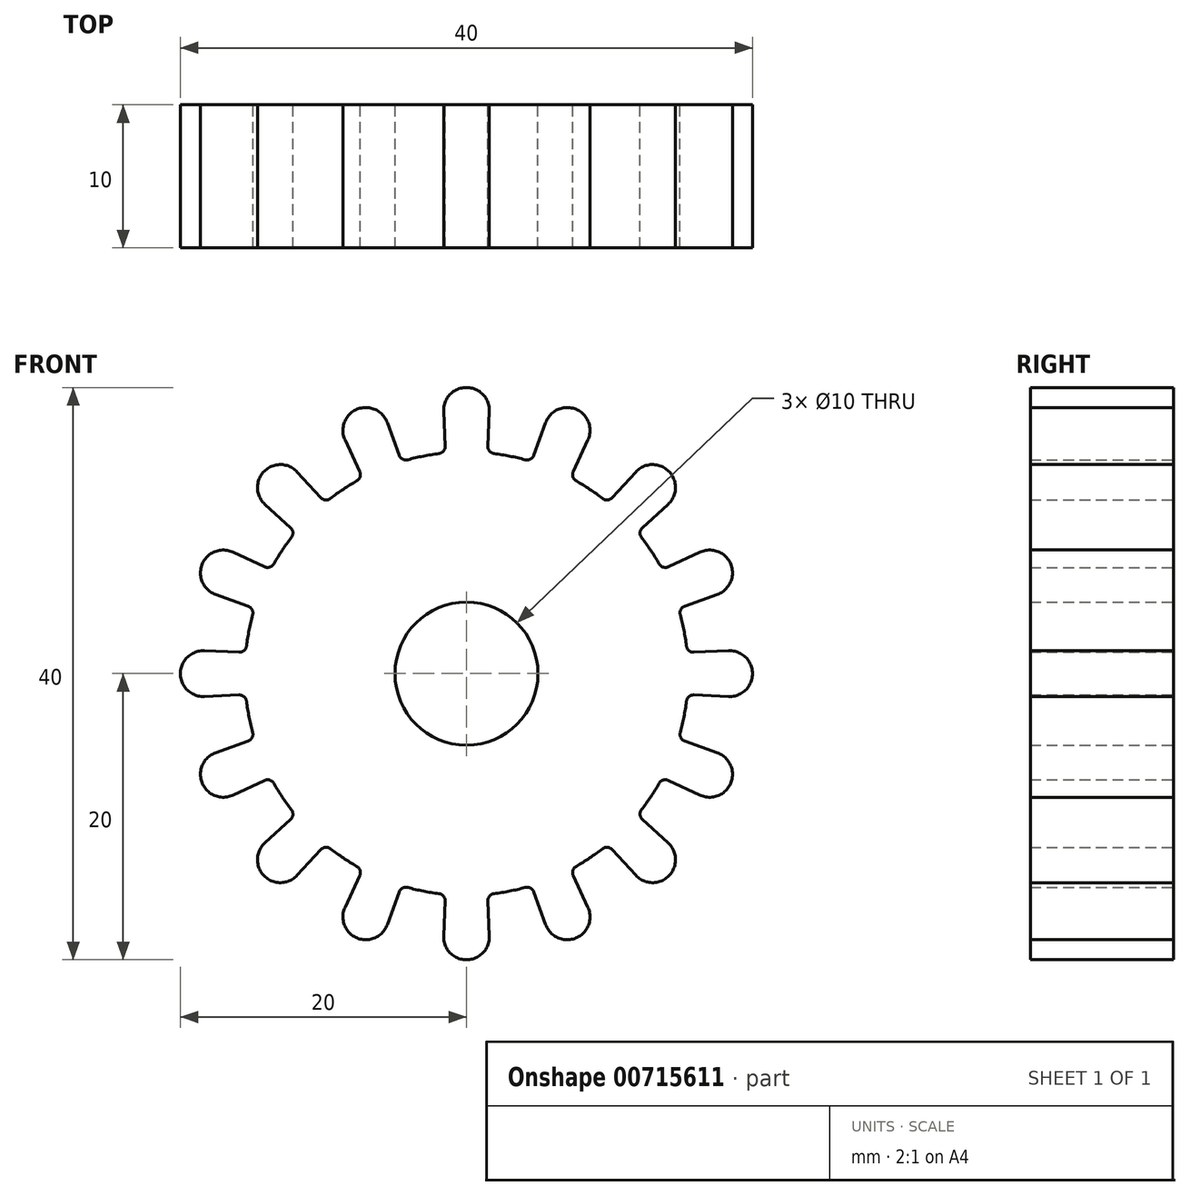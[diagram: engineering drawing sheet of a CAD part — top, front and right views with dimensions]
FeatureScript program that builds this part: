
annotation { "Feature Type Name" : "Feature", "Feature Type Description" : "" }
export const myFeature = defineFeature(function(context is Context, id is Id, definition is map)
    precondition{}
    {
        {
            var Q0;
            Q0=qCreatedBy(makeId("Front.planeOp"),FACE);
            var sketch = newSketch(context, id + "F0", { "sketchPlane" : qUnion([Q0])});
            skCircle(sketch, "E0", {"center": v(0, 0) * mm, "radius": 5 * mm});
            skCircle(sketch, "E1", {"center": v(0, 0) * mm, "radius": 15.5 * mm});
            skCircle(sketch, "E2", {"center": v(0, 0) * mm, "radius": 18.4 * mm, "construction": true});
            skCircle(sketch, "E3", {"center": v(0, 18.4) * mm, "radius": 1.6 * mm});
            skLineSegment(sketch, "E4", {"start": v(-1.6, 18.33) * mm, "end": v(-1.5, 15.9) * mm});
            skLineSegment(sketch, "E5", {"start": v(1.6, 18.33) * mm, "end": v(1.5, 15.9) * mm});
            skArc(sketch, "E6", {"start": v(-1.93, 15.38) * mm, "mid": v(-1.61, 15.55) * mm, "end": v(-1.5, 15.9) * mm});
            skArc(sketch, "E7", {"start": v(1.5, 15.9) * mm, "mid": v(1.61, 15.55) * mm, "end": v(1.93, 15.38) * mm});
            skCircle(sketch, "E8.1.0", {"center": v(-7.04, 17) * mm, "radius": 1.6 * mm});
            skLineSegment(sketch, "E8.1.1", {"start": v(-5.54, 17.55) * mm, "end": v(-4.7, 15.26) * mm});
            skLineSegment(sketch, "E8.1.2", {"start": v(-8.5, 16.32) * mm, "end": v(-7.46, 14.12) * mm});
            skArc(sketch, "E8.1.3", {"start": v(-7.67, 13.47) * mm, "mid": v(-7.44, 13.75) * mm, "end": v(-7.46, 14.12) * mm});
            skArc(sketch, "E8.1.4", {"start": v(-4.7, 15.26) * mm, "mid": v(-4.46, 14.99) * mm, "end": v(-4.1, 14.95) * mm});
            skCircle(sketch, "E8.2.0", {"center": v(-13.01, 13.01) * mm, "radius": 1.6 * mm});
            skLineSegment(sketch, "E8.2.1", {"start": v(-11.83, 14.1) * mm, "end": v(-10.19, 12.3) * mm});
            skLineSegment(sketch, "E8.2.2", {"start": v(-14.1, 11.83) * mm, "end": v(-12.3, 10.19) * mm});
            skArc(sketch, "E8.2.3", {"start": v(-12.24, 9.51) * mm, "mid": v(-12.14, 9.86) * mm, "end": v(-12.3, 10.19) * mm});
            skArc(sketch, "E8.2.4", {"start": v(-10.19, 12.3) * mm, "mid": v(-9.86, 12.14) * mm, "end": v(-9.51, 12.24) * mm});
            skCircle(sketch, "E9.1.3.0", {"center": v(-17, 7.04) * mm, "radius": 1.6 * mm});
            skLineSegment(sketch, "E9.2.3.0", {"start": v(-16.32, 8.5) * mm, "end": v(-14.12, 7.46) * mm});
            skLineSegment(sketch, "E9.5.3.0", {"start": v(-17.55, 5.54) * mm, "end": v(-15.26, 4.7) * mm});
            skArc(sketch, "E9.8.3.0", {"start": v(-14.95, 4.1) * mm, "mid": v(-14.99, 4.46) * mm, "end": v(-15.26, 4.7) * mm});
            skArc(sketch, "E9.12.3.0", {"start": v(-14.12, 7.46) * mm, "mid": v(-13.75, 7.44) * mm, "end": v(-13.47, 7.67) * mm});
            skCircle(sketch, "E9.1.4.0", {"center": v(-18.4, 0) * mm, "radius": 1.6 * mm});
            skLineSegment(sketch, "E9.2.4.0", {"start": v(-18.33, 1.6) * mm, "end": v(-15.9, 1.5) * mm});
            skLineSegment(sketch, "E9.5.4.0", {"start": v(-18.33, -1.6) * mm, "end": v(-15.9, -1.5) * mm});
            skArc(sketch, "E9.8.4.0", {"start": v(-15.38, -1.93) * mm, "mid": v(-15.55, -1.61) * mm, "end": v(-15.9, -1.5) * mm});
            skArc(sketch, "E9.12.4.0", {"start": v(-15.9, 1.5) * mm, "mid": v(-15.55, 1.61) * mm, "end": v(-15.38, 1.93) * mm});
            skCircle(sketch, "E9.1.5.0", {"center": v(-17, -7.04) * mm, "radius": 1.6 * mm});
            skLineSegment(sketch, "E9.2.5.0", {"start": v(-17.55, -5.54) * mm, "end": v(-15.26, -4.7) * mm});
            skLineSegment(sketch, "E9.5.5.0", {"start": v(-16.32, -8.5) * mm, "end": v(-14.12, -7.46) * mm});
            skArc(sketch, "E9.8.5.0", {"start": v(-13.47, -7.67) * mm, "mid": v(-13.75, -7.44) * mm, "end": v(-14.12, -7.46) * mm});
            skArc(sketch, "E9.12.5.0", {"start": v(-15.26, -4.7) * mm, "mid": v(-14.99, -4.46) * mm, "end": v(-14.95, -4.1) * mm});
            skCircle(sketch, "E9.1.6.0", {"center": v(-13.01, -13.01) * mm, "radius": 1.6 * mm});
            skLineSegment(sketch, "E9.2.6.0", {"start": v(-14.1, -11.83) * mm, "end": v(-12.3, -10.19) * mm});
            skLineSegment(sketch, "E9.5.6.0", {"start": v(-11.83, -14.1) * mm, "end": v(-10.19, -12.3) * mm});
            skArc(sketch, "E9.8.6.0", {"start": v(-9.51, -12.24) * mm, "mid": v(-9.86, -12.14) * mm, "end": v(-10.19, -12.3) * mm});
            skArc(sketch, "E9.12.6.0", {"start": v(-12.3, -10.19) * mm, "mid": v(-12.14, -9.86) * mm, "end": v(-12.24, -9.51) * mm});
            skCircle(sketch, "E9.1.7.0", {"center": v(-7.04, -17) * mm, "radius": 1.6 * mm});
            skLineSegment(sketch, "E9.2.7.0", {"start": v(-8.5, -16.32) * mm, "end": v(-7.46, -14.12) * mm});
            skLineSegment(sketch, "E9.5.7.0", {"start": v(-5.54, -17.55) * mm, "end": v(-4.7, -15.26) * mm});
            skArc(sketch, "E9.8.7.0", {"start": v(-4.1, -14.95) * mm, "mid": v(-4.46, -14.99) * mm, "end": v(-4.7, -15.26) * mm});
            skArc(sketch, "E9.12.7.0", {"start": v(-7.46, -14.12) * mm, "mid": v(-7.44, -13.75) * mm, "end": v(-7.67, -13.47) * mm});
            skCircle(sketch, "E9.1.8.0", {"center": v(0, -18.4) * mm, "radius": 1.6 * mm});
            skLineSegment(sketch, "E9.2.8.0", {"start": v(-1.6, -18.33) * mm, "end": v(-1.5, -15.9) * mm});
            skLineSegment(sketch, "E9.5.8.0", {"start": v(1.6, -18.33) * mm, "end": v(1.5, -15.9) * mm});
            skArc(sketch, "E9.8.8.0", {"start": v(1.93, -15.38) * mm, "mid": v(1.61, -15.55) * mm, "end": v(1.5, -15.9) * mm});
            skArc(sketch, "E9.12.8.0", {"start": v(-1.5, -15.9) * mm, "mid": v(-1.61, -15.55) * mm, "end": v(-1.93, -15.38) * mm});
            skCircle(sketch, "E9.1.9.0", {"center": v(7.04, -17) * mm, "radius": 1.6 * mm});
            skLineSegment(sketch, "E9.2.9.0", {"start": v(5.54, -17.55) * mm, "end": v(4.7, -15.26) * mm});
            skLineSegment(sketch, "E9.5.9.0", {"start": v(8.5, -16.32) * mm, "end": v(7.46, -14.12) * mm});
            skArc(sketch, "E9.8.9.0", {"start": v(7.67, -13.47) * mm, "mid": v(7.44, -13.75) * mm, "end": v(7.46, -14.12) * mm});
            skArc(sketch, "E9.12.9.0", {"start": v(4.7, -15.26) * mm, "mid": v(4.46, -14.99) * mm, "end": v(4.1, -14.95) * mm});
            skCircle(sketch, "E9.1.10.0", {"center": v(13.01, -13.01) * mm, "radius": 1.6 * mm});
            skLineSegment(sketch, "E9.2.10.0", {"start": v(11.83, -14.1) * mm, "end": v(10.19, -12.3) * mm});
            skLineSegment(sketch, "E9.5.10.0", {"start": v(14.1, -11.83) * mm, "end": v(12.3, -10.19) * mm});
            skArc(sketch, "E9.8.10.0", {"start": v(12.24, -9.51) * mm, "mid": v(12.14, -9.86) * mm, "end": v(12.3, -10.19) * mm});
            skArc(sketch, "E9.12.10.0", {"start": v(10.19, -12.3) * mm, "mid": v(9.86, -12.14) * mm, "end": v(9.51, -12.24) * mm});
            skCircle(sketch, "E9.1.11.0", {"center": v(17, -7.04) * mm, "radius": 1.6 * mm});
            skLineSegment(sketch, "E9.2.11.0", {"start": v(16.32, -8.5) * mm, "end": v(14.12, -7.46) * mm});
            skLineSegment(sketch, "E9.5.11.0", {"start": v(17.55, -5.54) * mm, "end": v(15.26, -4.7) * mm});
            skArc(sketch, "E9.8.11.0", {"start": v(14.95, -4.1) * mm, "mid": v(14.99, -4.46) * mm, "end": v(15.26, -4.7) * mm});
            skArc(sketch, "E9.12.11.0", {"start": v(14.12, -7.46) * mm, "mid": v(13.75, -7.44) * mm, "end": v(13.47, -7.67) * mm});
            skCircle(sketch, "E9.1.12.0", {"center": v(18.4, 0) * mm, "radius": 1.6 * mm});
            skLineSegment(sketch, "E9.2.12.0", {"start": v(18.33, -1.6) * mm, "end": v(15.9, -1.5) * mm});
            skLineSegment(sketch, "E9.5.12.0", {"start": v(18.33, 1.6) * mm, "end": v(15.9, 1.5) * mm});
            skArc(sketch, "E9.8.12.0", {"start": v(15.38, 1.93) * mm, "mid": v(15.55, 1.61) * mm, "end": v(15.9, 1.5) * mm});
            skArc(sketch, "E9.12.12.0", {"start": v(15.9, -1.5) * mm, "mid": v(15.55, -1.61) * mm, "end": v(15.38, -1.93) * mm});
            skCircle(sketch, "E9.1.13.0", {"center": v(17, 7.04) * mm, "radius": 1.6 * mm});
            skLineSegment(sketch, "E9.2.13.0", {"start": v(17.55, 5.54) * mm, "end": v(15.26, 4.7) * mm});
            skLineSegment(sketch, "E9.5.13.0", {"start": v(16.32, 8.5) * mm, "end": v(14.12, 7.46) * mm});
            skArc(sketch, "E9.8.13.0", {"start": v(13.47, 7.67) * mm, "mid": v(13.75, 7.44) * mm, "end": v(14.12, 7.46) * mm});
            skArc(sketch, "E9.12.13.0", {"start": v(15.26, 4.7) * mm, "mid": v(14.99, 4.46) * mm, "end": v(14.95, 4.1) * mm});
            skCircle(sketch, "E9.1.14.0", {"center": v(13.01, 13.01) * mm, "radius": 1.6 * mm});
            skLineSegment(sketch, "E9.2.14.0", {"start": v(14.1, 11.83) * mm, "end": v(12.3, 10.19) * mm});
            skLineSegment(sketch, "E9.5.14.0", {"start": v(11.83, 14.1) * mm, "end": v(10.19, 12.3) * mm});
            skArc(sketch, "E9.8.14.0", {"start": v(9.51, 12.24) * mm, "mid": v(9.86, 12.14) * mm, "end": v(10.19, 12.3) * mm});
            skArc(sketch, "E9.12.14.0", {"start": v(12.3, 10.19) * mm, "mid": v(12.14, 9.86) * mm, "end": v(12.24, 9.51) * mm});
            skCircle(sketch, "E9.1.15.0", {"center": v(7.04, 17) * mm, "radius": 1.6 * mm});
            skLineSegment(sketch, "E9.2.15.0", {"start": v(8.5, 16.32) * mm, "end": v(7.46, 14.12) * mm});
            skLineSegment(sketch, "E9.5.15.0", {"start": v(5.54, 17.55) * mm, "end": v(4.7, 15.26) * mm});
            skArc(sketch, "E9.8.15.0", {"start": v(4.1, 14.95) * mm, "mid": v(4.46, 14.99) * mm, "end": v(4.7, 15.26) * mm});
            skArc(sketch, "E9.12.15.0", {"start": v(7.46, 14.12) * mm, "mid": v(7.44, 13.75) * mm, "end": v(7.67, 13.47) * mm});
            skSolve(sketch);
        }
        {
            var Q0;
            Q0 = qSketchRegion(id + "F0", true);
            extrude(context, id + "F1", {"entities" : qUnion([Q0]), "depth" : 10 * mm, "offsetDistance" : 25 * mm});
        }
    });
